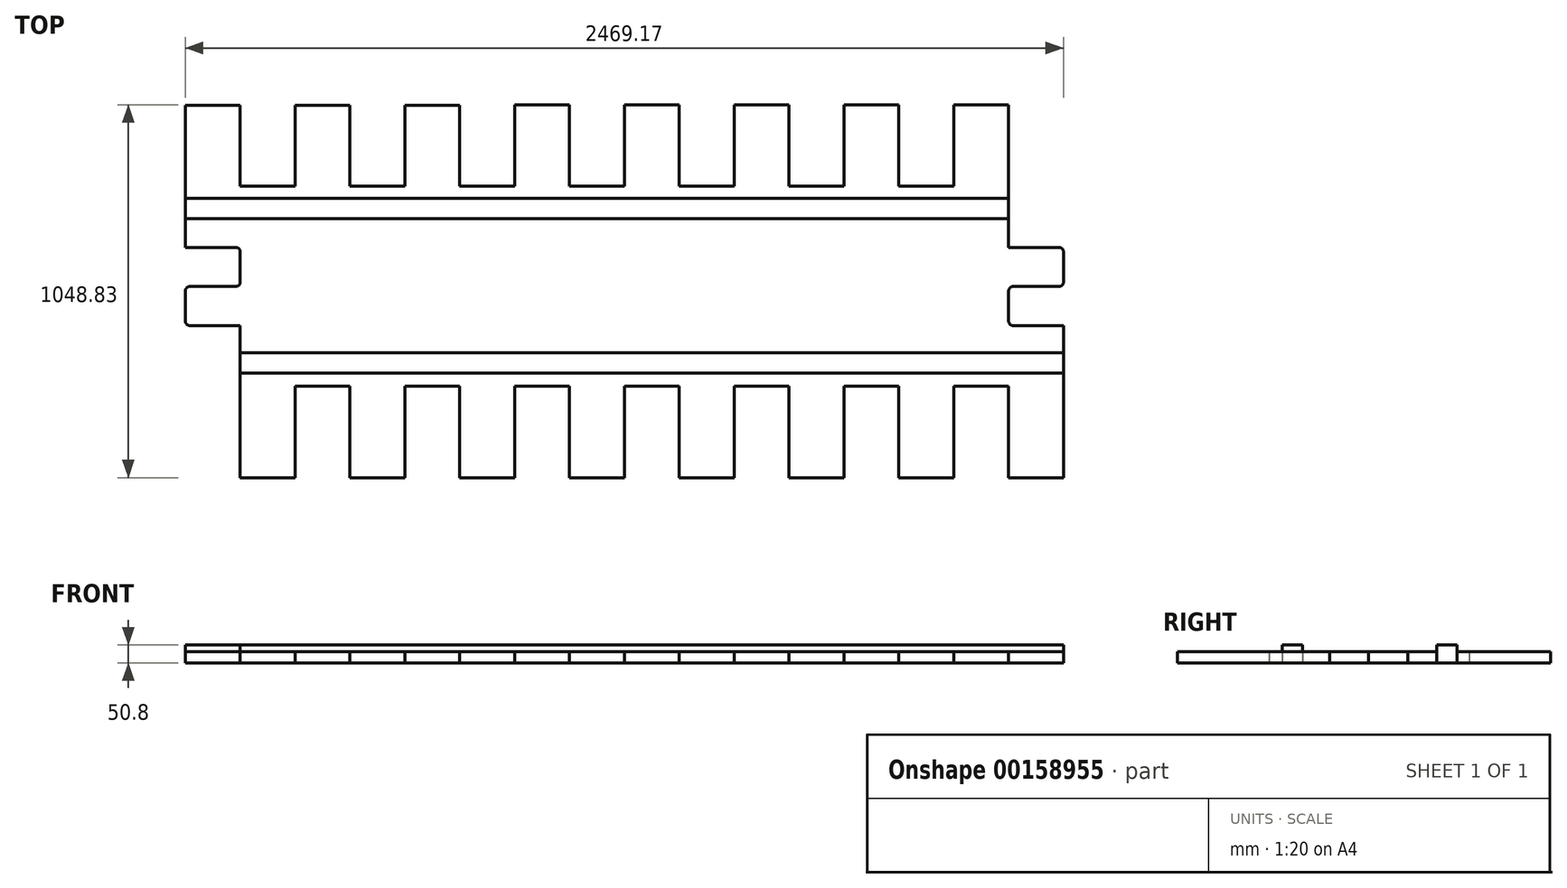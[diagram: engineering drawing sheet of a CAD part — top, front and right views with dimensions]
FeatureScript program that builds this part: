
annotation { "Feature Type Name" : "Feature", "Feature Type Description" : "" }
export const myFeature = defineFeature(function(context is Context, id is Id, definition is map)
    precondition{}
    {
        {
            var Q0;
            Q0=qCreatedBy(makeId("Top.planeOp"),FACE);
            var sketch = newSketch(context, id + "F0", { "sketchPlane" : qUnion([Q0])});
            skLineSegment(sketch, "E0", {"start": v(0, 0) * mm, "end": v(141.6, 0) * mm});
            skLineSegment(sketch, "E1", {"start": v(154.3, -12.7) * mm, "end": v(154.3, -97.3) * mm});
            skLineSegment(sketch, "E2", {"start": v(141.6, -110) * mm, "end": v(12.7, -110) * mm});
            skLineSegment(sketch, "E3", {"start": v(0, -122.7) * mm, "end": v(0, -207.32) * mm});
            skLineSegment(sketch, "E4", {"start": v(12.7, -220.02) * mm, "end": v(154.3, -220.02) * mm});
            skLineSegment(sketch, "E5", {"start": v(154.3, -220.02) * mm, "end": v(154.3, -647.87) * mm});
            skLineSegment(sketch, "E6", {"start": v(154.3, -647.87) * mm, "end": v(0, -647.87) * mm});
            skLineSegment(sketch, "E7", {"start": v(0, -647.87) * mm, "end": v(0, -389.82) * mm});
            skLineSegment(sketch, "E8", {"start": v(0, -389.82) * mm, "end": v(-154.3, -389.82) * mm});
            skLineSegment(sketch, "E9", {"start": v(-154.3, -389.82) * mm, "end": v(-154.3, -647.87) * mm});
            skLineSegment(sketch, "E10", {"start": v(-154.3, -647.87) * mm, "end": v(-308.61, -647.87) * mm});
            skLineSegment(sketch, "E11", {"start": v(-308.61, -647.87) * mm, "end": v(-308.61, -389.82) * mm});
            skLineSegment(sketch, "E12", {"start": v(-308.61, -389.82) * mm, "end": v(-462.92, -389.82) * mm});
            skLineSegment(sketch, "E13", {"start": v(-462.92, -389.82) * mm, "end": v(-462.92, -647.87) * mm});
            skLineSegment(sketch, "E14", {"start": v(-462.92, -647.87) * mm, "end": v(-617.22, -647.87) * mm});
            skLineSegment(sketch, "E15", {"start": v(-617.22, -647.87) * mm, "end": v(-617.22, -389.82) * mm});
            skLineSegment(sketch, "E16", {"start": v(-617.22, -389.82) * mm, "end": v(-771.53, -389.82) * mm});
            skLineSegment(sketch, "E17", {"start": v(-771.53, -389.82) * mm, "end": v(-771.53, -647.87) * mm});
            skLineSegment(sketch, "E18", {"start": v(-771.53, -647.87) * mm, "end": v(-925.83, -647.87) * mm});
            skLineSegment(sketch, "E19", {"start": v(-925.83, -647.87) * mm, "end": v(-925.83, -389.82) * mm});
            skPoint(sketch, "E20.visualSharp", {"position": v(154.3, 0) * mm});
            skArc(sketch, "E20.filletArc", {"start": v(154.3, -12.7) * mm, "mid": v(150.59, -3.72) * mm, "end": v(141.6, 0) * mm});
            skPoint(sketch, "E21.visualSharp", {"position": v(154.3, -110) * mm});
            skArc(sketch, "E21.filletArc", {"start": v(141.6, -110) * mm, "mid": v(150.59, -106.29) * mm, "end": v(154.3, -97.3) * mm});
            skPoint(sketch, "E22.visualSharp", {"position": v(0, -220.02) * mm});
            skArc(sketch, "E22.filletArc", {"start": v(0, -207.32) * mm, "mid": v(3.72, -216.3) * mm, "end": v(12.7, -220.02) * mm});
            skPoint(sketch, "E23.visualSharp", {"position": v(0, -110) * mm});
            skArc(sketch, "E23.filletArc", {"start": v(12.7, -110) * mm, "mid": v(3.72, -113.73) * mm, "end": v(0, -122.7) * mm});
            skLineSegment(sketch, "E24", {"start": v(-925.83, -389.82) * mm, "end": v(-1080.14, -389.82) * mm});
            skLineSegment(sketch, "E25", {"start": v(-1080.14, -389.82) * mm, "end": v(-1080.14, -647.87) * mm});
            skLineSegment(sketch, "E26", {"start": v(-1080.14, -647.87) * mm, "end": v(-1234.44, -647.87) * mm});
            skLineSegment(sketch, "E27", {"start": v(-1234.44, -647.87) * mm, "end": v(-1234.44, -389.82) * mm});
            skLineSegment(sketch, "E28", {"start": v(-1234.44, -389.82) * mm, "end": v(-1388.75, -389.82) * mm});
            skLineSegment(sketch, "E29", {"start": v(-1388.75, -389.82) * mm, "end": v(-1388.75, -647.87) * mm});
            skLineSegment(sketch, "E30", {"start": v(-1388.75, -647.87) * mm, "end": v(-1543.05, -647.87) * mm});
            skLineSegment(sketch, "E31", {"start": v(-1543.05, -647.87) * mm, "end": v(-1543.05, -389.82) * mm});
            skLineSegment(sketch, "E32", {"start": v(-1543.05, -389.82) * mm, "end": v(-1697.36, -389.82) * mm});
            skLineSegment(sketch, "E33", {"start": v(-1697.36, -389.82) * mm, "end": v(-1697.36, -647.87) * mm});
            skLineSegment(sketch, "E34", {"start": v(-1697.36, -647.87) * mm, "end": v(-1851.67, -647.87) * mm});
            skLineSegment(sketch, "E35", {"start": v(-1851.67, -647.87) * mm, "end": v(-1851.67, -389.82) * mm});
            skLineSegment(sketch, "E36", {"start": v(-1851.67, -389.82) * mm, "end": v(-2005.97, -389.82) * mm});
            skLineSegment(sketch, "E37", {"start": v(-2005.97, -389.82) * mm, "end": v(-2005.97, -647.87) * mm});
            skLineSegment(sketch, "E38", {"start": v(-2005.97, -647.87) * mm, "end": v(-2160.29, -647.87) * mm});
            skLineSegment(sketch, "E39", {"start": v(-2160.29, -647.87) * mm, "end": v(-2160.29, -220.02) * mm});
            skLineSegment(sketch, "E40", {"start": v(-2160.29, -220.02) * mm, "end": v(-2301.9, -220.02) * mm});
            skLineSegment(sketch, "E41", {"start": v(-2314.6, -207.32) * mm, "end": v(-2314.6, -122.7) * mm});
            skLineSegment(sketch, "E42", {"start": v(-2301.9, -110) * mm, "end": v(-2172.99, -110) * mm});
            skLineSegment(sketch, "E43", {"start": v(-2160.29, -97.3) * mm, "end": v(-2160.29, -12.7) * mm});
            skLineSegment(sketch, "E44", {"start": v(-2172.99, 0) * mm, "end": v(-2314.6, 0) * mm});
            skLineSegment(sketch, "E45", {"start": v(-2314.6, 0) * mm, "end": v(-2314.6, 399.88) * mm});
            skPoint(sketch, "E46.visualSharp", {"position": v(-2314.6, -110) * mm});
            skArc(sketch, "E46.filletArc", {"start": v(-2301.9, -110) * mm, "mid": v(-2310.87, -113.73) * mm, "end": v(-2314.6, -122.7) * mm});
            skPoint(sketch, "E47.visualSharp", {"position": v(-2314.6, -220.02) * mm});
            skArc(sketch, "E47.filletArc", {"start": v(-2314.6, -207.32) * mm, "mid": v(-2310.87, -216.3) * mm, "end": v(-2301.9, -220.02) * mm});
            skPoint(sketch, "E48.visualSharp", {"position": v(-2160.29, -110) * mm});
            skArc(sketch, "E48.filletArc", {"start": v(-2172.99, -110) * mm, "mid": v(-2164, -106.29) * mm, "end": v(-2160.29, -97.3) * mm});
            skPoint(sketch, "E49.visualSharp", {"position": v(-2160.29, 0) * mm});
            skArc(sketch, "E49.filletArc", {"start": v(-2160.29, -12.7) * mm, "mid": v(-2164, -3.72) * mm, "end": v(-2172.99, 0) * mm});
            skLineSegment(sketch, "E50", {"start": v(-2314.6, 399.88) * mm, "end": v(-2160.29, 399.88) * mm});
            skLineSegment(sketch, "E51", {"start": v(-2160.29, 399.88) * mm, "end": v(-2160.29, 172.14) * mm});
            skLineSegment(sketch, "E52", {"start": v(-2160.29, 172.14) * mm, "end": v(-2005.98, 172.14) * mm});
            skLineSegment(sketch, "E53", {"start": v(-2005.98, 172.14) * mm, "end": v(-2005.98, 399.88) * mm});
            skLineSegment(sketch, "E54", {"start": v(-2005.98, 399.88) * mm, "end": v(-1851.68, 399.88) * mm});
            skLineSegment(sketch, "E55", {"start": v(-1851.68, 399.88) * mm, "end": v(-1851.68, 172.14) * mm});
            skLineSegment(sketch, "E56", {"start": v(-1851.68, 172.14) * mm, "end": v(-1697.37, 172.14) * mm});
            skLineSegment(sketch, "E57", {"start": v(-1697.37, 172.14) * mm, "end": v(-1697.37, 399.88) * mm});
            skLineSegment(sketch, "E58", {"start": v(-1697.37, 399.88) * mm, "end": v(-1543.07, 399.88) * mm});
            skLineSegment(sketch, "E59", {"start": v(-1543.07, 399.88) * mm, "end": v(-1543.07, 172.14) * mm});
            skLineSegment(sketch, "E60", {"start": v(-1543.07, 172.14) * mm, "end": v(-1388.76, 172.14) * mm});
            skLineSegment(sketch, "E61", {"start": v(-1388.76, 172.14) * mm, "end": v(-1388.76, 400.96) * mm});
            skLineSegment(sketch, "E62", {"start": v(-1388.76, 400.96) * mm, "end": v(-1234.46, 400.96) * mm});
            skLineSegment(sketch, "E63", {"start": v(-1234.46, 400.96) * mm, "end": v(-1234.46, 172.14) * mm});
            skLineSegment(sketch, "E64", {"start": v(-1234.46, 172.14) * mm, "end": v(-1080.15, 172.14) * mm});
            skLineSegment(sketch, "E65", {"start": v(-1080.15, 172.14) * mm, "end": v(-1080.15, 400.96) * mm});
            skLineSegment(sketch, "E66", {"start": v(-1080.15, 400.96) * mm, "end": v(-925.85, 400.96) * mm});
            skLineSegment(sketch, "E67", {"start": v(-925.85, 400.96) * mm, "end": v(-925.85, 172.14) * mm});
            skLineSegment(sketch, "E68", {"start": v(-925.85, 172.14) * mm, "end": v(-771.54, 172.14) * mm});
            skLineSegment(sketch, "E69", {"start": v(-771.54, 172.14) * mm, "end": v(-771.54, 400.96) * mm});
            skLineSegment(sketch, "E70", {"start": v(-771.54, 400.96) * mm, "end": v(-617.24, 400.96) * mm});
            skLineSegment(sketch, "E71", {"start": v(-617.24, 400.96) * mm, "end": v(-617.24, 172.14) * mm});
            skLineSegment(sketch, "E72", {"start": v(-617.24, 172.14) * mm, "end": v(-462.93, 172.14) * mm});
            skLineSegment(sketch, "E73", {"start": v(-462.93, 172.14) * mm, "end": v(-462.93, 400.96) * mm});
            skLineSegment(sketch, "E74", {"start": v(-462.93, 400.96) * mm, "end": v(-308.63, 400.96) * mm});
            skLineSegment(sketch, "E75", {"start": v(-308.63, 400.96) * mm, "end": v(-308.63, 172.14) * mm});
            skLineSegment(sketch, "E76", {"start": v(-308.63, 172.14) * mm, "end": v(-154.32, 172.14) * mm});
            skLineSegment(sketch, "E77", {"start": v(-154.32, 172.14) * mm, "end": v(-154.32, 400.96) * mm});
            skLineSegment(sketch, "E78", {"start": v(-154.32, 400.96) * mm, "end": v(-0.02, 400.96) * mm});
            skLineSegment(sketch, "E79", {"start": v(-0.02, 400.96) * mm, "end": v(-0.02, 172.14) * mm});
            skLineSegment(sketch, "E80", {"start": v(-0.02, 172.14) * mm, "end": v(0, 0) * mm});
            skSolve(sketch);
        }
        {
            var Q0;
            Q0=makeQuery(id+"F0.imprint","IMPRINT",FACE,{"disambiguationData":[TD([[makeQuery(id+"F0.imprint","IMPRINT",EDGE,{"derivedFrom":sQuery(id+"F0.wireOp",EDGE,"E0")}),-1.0]])]});
            var sketch = newSketch(context, id + "F1", { "sketchPlane" : qUnion([Q0])});
            skLineSegment(sketch, "E81", {"start": v(-2314.86, 138.26) * mm, "end": v(0, 138.26) * mm});
            skLineSegment(sketch, "E82.0", {"start": v(-2314.86, 81.11) * mm, "end": v(0, 81.11) * mm});
            skLineSegment(sketch, "E83", {"start": v(-2160.59, -353.29) * mm, "end": v(154.12, -353.29) * mm});
            skLineSegment(sketch, "E84.0", {"start": v(-2160.59, -296.14) * mm, "end": v(154.12, -296.14) * mm});
            skLineSegment(sketch, "E85", {"start": v(-2314.86, 138.26) * mm, "end": v(-2314.86, 81.11) * mm});
            skLineSegment(sketch, "E86", {"start": v(-2160.59, -296.14) * mm, "end": v(-2160.59, -353.29) * mm});
            skLineSegment(sketch, "E87", {"start": v(154.12, -296.14) * mm, "end": v(154.12, -353.29) * mm});
            skLineSegment(sketch, "E88", {"start": v(0, 138.26) * mm, "end": v(0, 81.11) * mm});
            skSolve(sketch);
        }
        {
            var Q0;
            Q0=qSketchRegion(id+"F0",true);
            extrude(context, id + "F2", {"entities" : qUnion([Q0]), "depth" : 31.75 * mm});
        }
        {
            var Q0;
            Q0=qSketchRegion(id+"F1",true);
            extrude(context, id + "F3", {"entities" : qUnion([Q0]), "operationType" : NewBodyOperationType.ADD, "depth" : 50.8 * mm});
        }
    });
